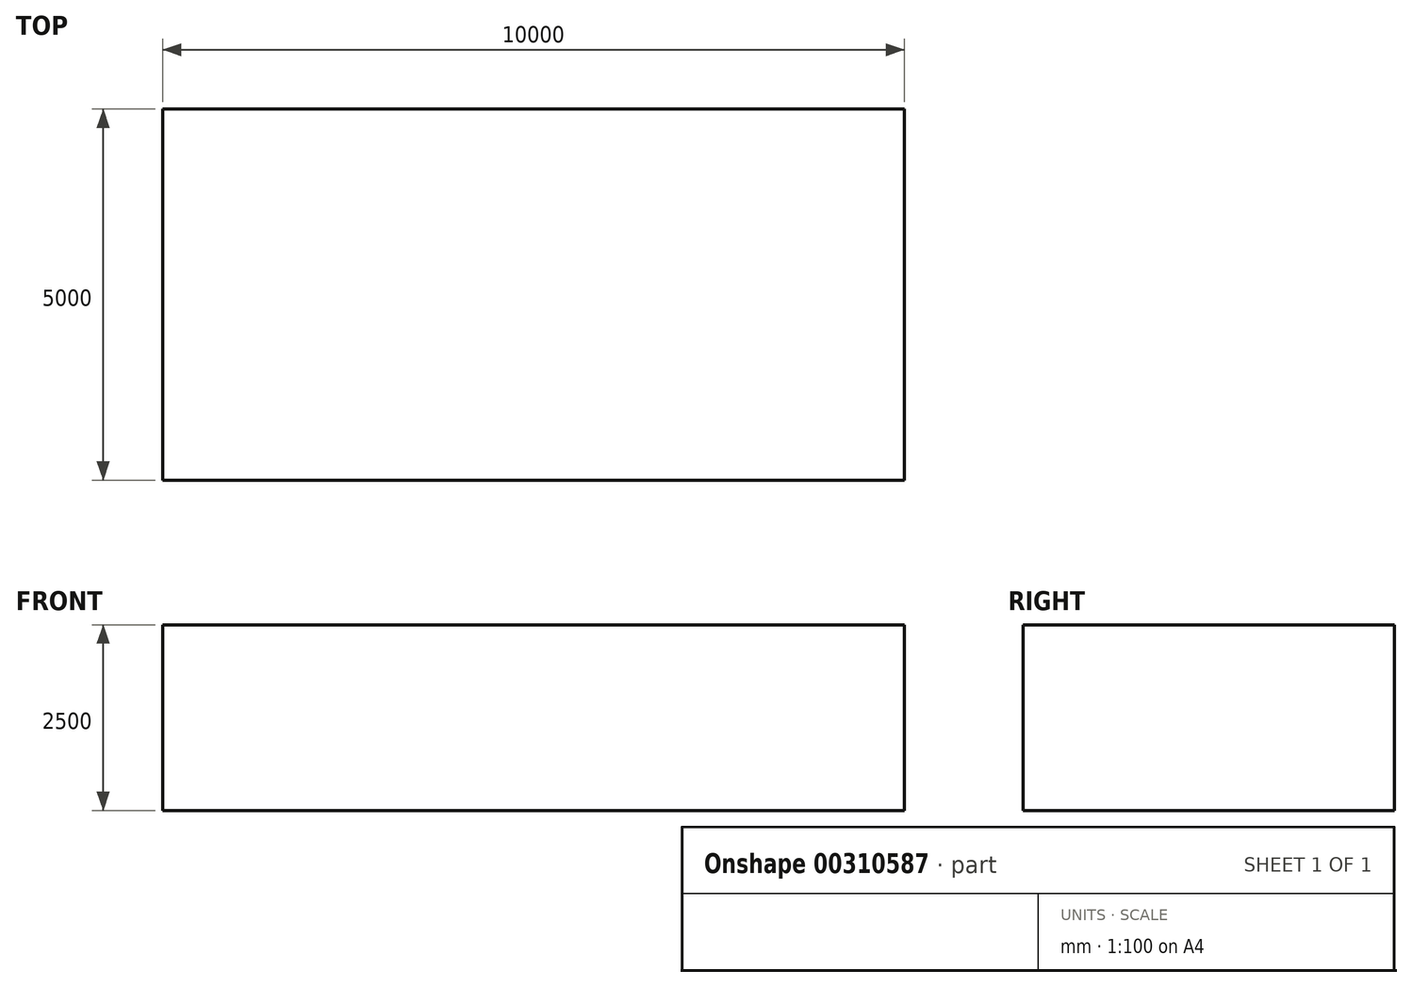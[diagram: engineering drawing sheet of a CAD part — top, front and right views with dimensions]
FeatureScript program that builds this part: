
annotation { "Feature Type Name" : "Feature", "Feature Type Description" : "" }
export const myFeature = defineFeature(function(context is Context, id is Id, definition is map)
    precondition{}
    {
        {
            var Q0;
            Q0=qCreatedBy(makeId("Front.planeOp"),FACE);
            var sketch = newSketch(context, id + "F0", { "sketchPlane" : qUnion([Q0])});
            skLineSegment(sketch, "E0", {"start": v(0, 0) * mm, "end": v(10000, 0) * mm});
            skLineSegment(sketch, "E1", {"start": v(0, 0) * mm, "end": v(0, 2500) * mm});
            skLineSegment(sketch, "E2", {"start": v(0, 2500) * mm, "end": v(10000, 2500) * mm});
            skLineSegment(sketch, "E3", {"start": v(10000, 0) * mm, "end": v(10000, 2500) * mm});
            skSolve(sketch);
        }
        {
            var Q0;
            Q0=makeQuery(id+"F0.imprint","IMPRINT",FACE,{"disambiguationData":[TD([[makeQuery(id+"F0.imprint","IMPRINT",EDGE,{"derivedFrom":sQuery(id+"F0.wireOp",EDGE,"E0")}),1.0]])]});
            extrude(context, id + "F1", {"entities" : qUnion([Q0]), "depth" : 5000 * mm});
        }
    });
